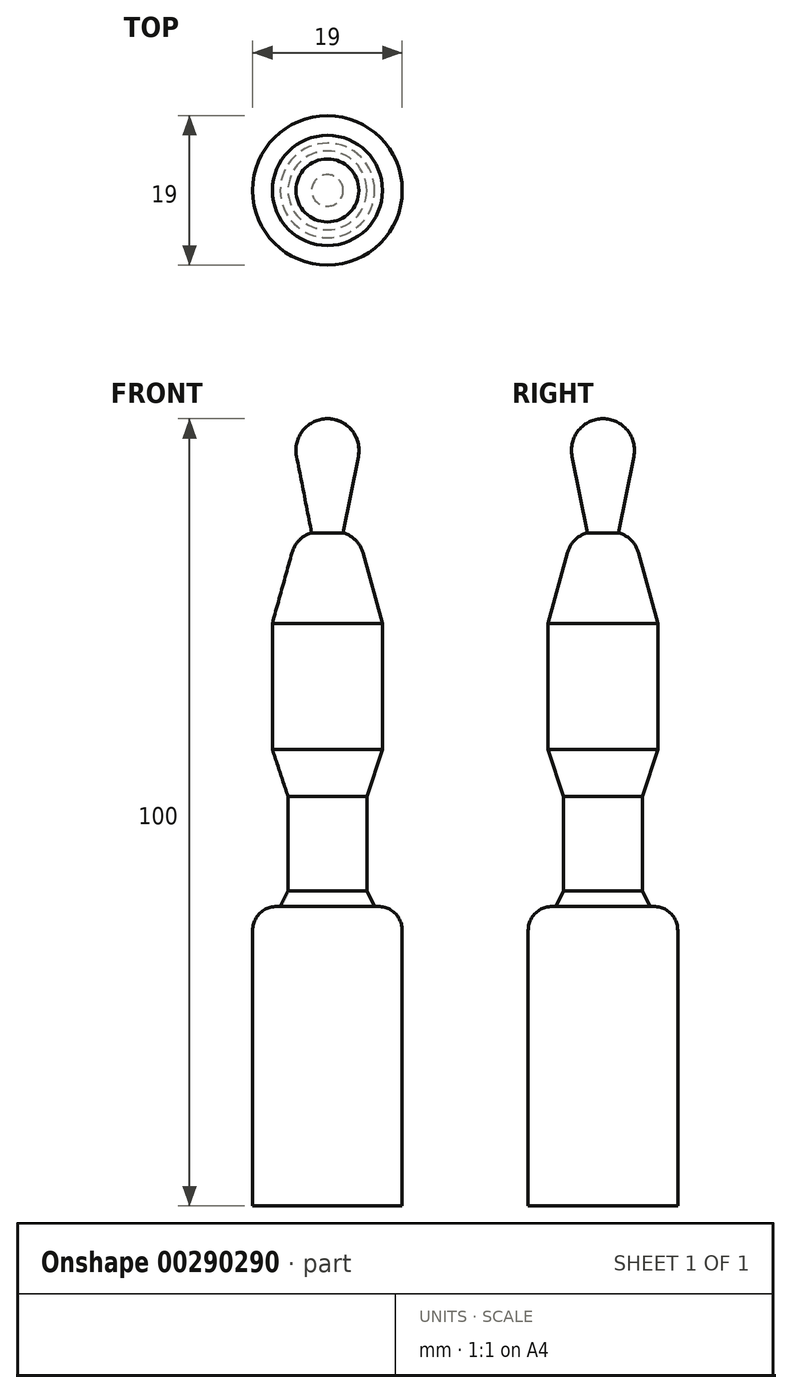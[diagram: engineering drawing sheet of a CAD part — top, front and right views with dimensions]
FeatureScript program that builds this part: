
annotation { "Feature Type Name" : "Feature", "Feature Type Description" : "" }
export const myFeature = defineFeature(function(context is Context, id is Id, definition is map)
    precondition{}
    {
        {
            var Q0;
            Q0=qCreatedBy(makeId("Front.planeOp"),FACE);
            var sketch = newSketch(context, id + "F0", { "sketchPlane" : qUnion([Q0])});
            skArc(sketch, "E0", {"start": v(3.92, -4.78) * mm, "mid": v(3.1, -1.46) * mm, "end": v(0, 0) * mm});
            skLineSegment(sketch, "E1", {"start": v(3.92, -4.78) * mm, "end": v(2, -14.5) * mm});
            skArc(sketch, "E2", {"start": v(4.5, -17) * mm, "mid": v(3.58, -15.42) * mm, "end": v(2, -14.5) * mm});
            skLineSegment(sketch, "E3", {"start": v(4.5, -17) * mm, "end": v(7, -26) * mm});
            skLineSegment(sketch, "E4", {"start": v(7, -26) * mm, "end": v(7, -42) * mm});
            skLineSegment(sketch, "E5", {"start": v(7, -42) * mm, "end": v(5, -48) * mm});
            skLineSegment(sketch, "E6", {"start": v(5, -48) * mm, "end": v(5, -60) * mm});
            skLineSegment(sketch, "E7", {"start": v(5, -60) * mm, "end": v(6, -62) * mm});
            skArc(sketch, "E8", {"start": v(9.5, -65) * mm, "mid": v(8.44, -62.7) * mm, "end": v(6, -62) * mm});
            skLineSegment(sketch, "E9", {"start": v(9.5, -65) * mm, "end": v(9.5, -100) * mm});
            skLineSegment(sketch, "E10", {"start": v(9.5, -100) * mm, "end": v(0, -100) * mm});
            skLineSegment(sketch, "E11", {"start": v(0, -100) * mm, "end": v(0, 0) * mm});
            skSolve(sketch);
        }
        {
            var Q0;
            Q0 = qSketchRegion(id + "F0", true);
            var Q1;
            Q1=sQuery(id+"F0.wireOp",EDGE,"E11");
            revolve(context, id + "F1", {"entities" : qUnion([Q0]), "axis" : qUnion([Q1]), "revolveType" : RevolveType.FULL});
        }
    });
